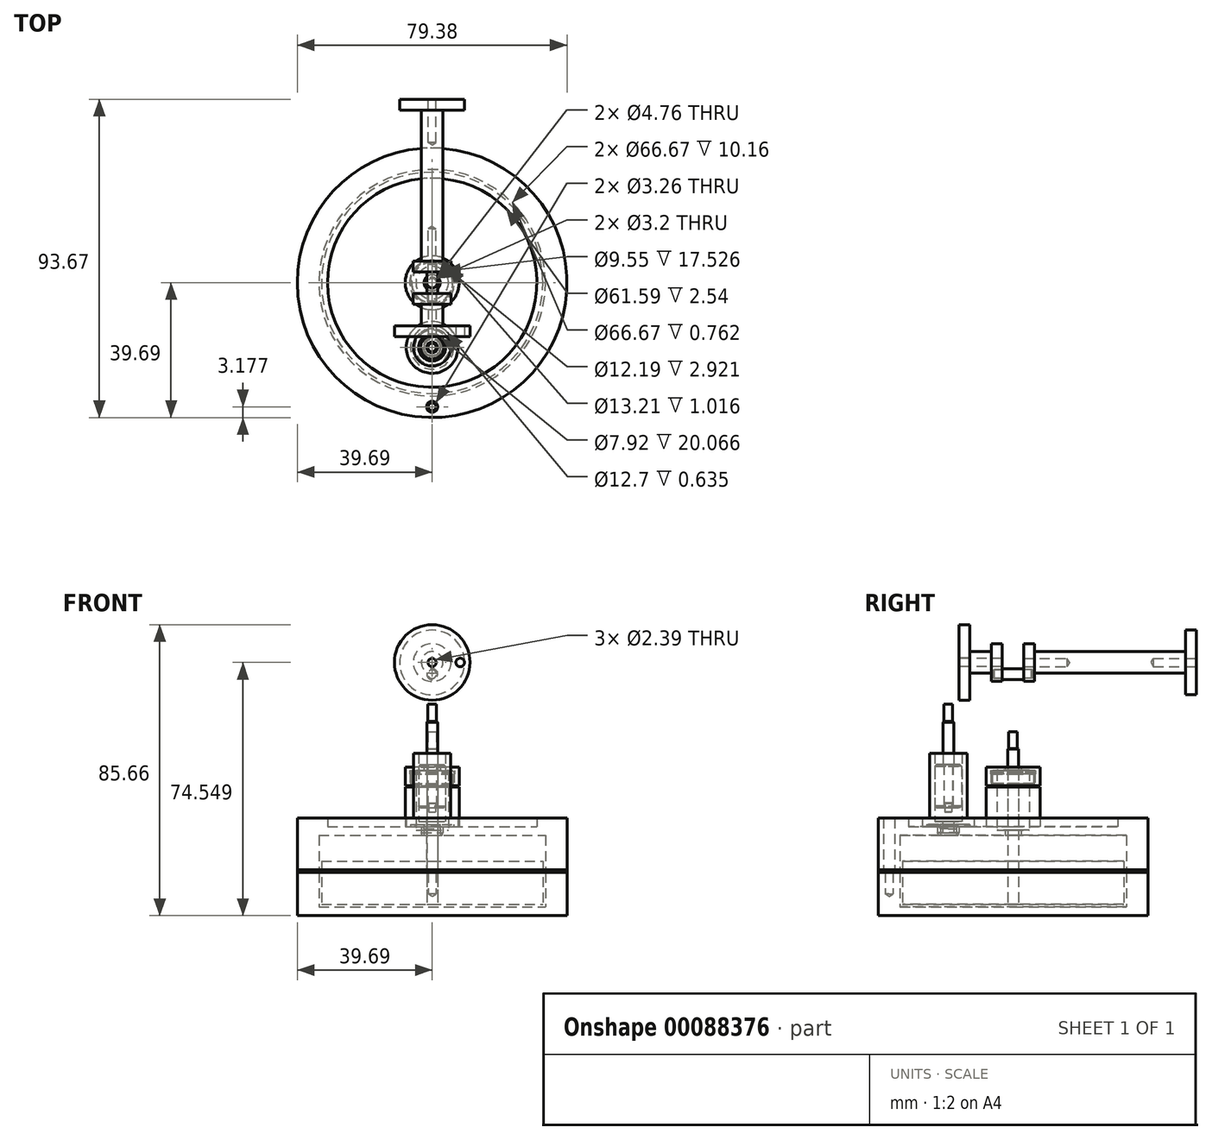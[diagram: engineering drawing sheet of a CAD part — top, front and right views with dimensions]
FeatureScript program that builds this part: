
annotation { "Feature Type Name" : "Feature", "Feature Type Description" : "" }
export const myFeature = defineFeature(function(context is Context, id is Id, definition is map)
    precondition{}
    {
        {
            assignVariable(context, id + "F0", {"name" : "RevolveDeg", "anyValue" : 360});
        }
        {
            var Q0;
            Q0=qCreatedBy(makeId("Right.planeOp"),FACE);
            var sketch = newSketch(context, id + "F1", { "sketchPlane" : qUnion([Q0])});
            skLineSegment(sketch, "E0", {"start": v(0, 0) * mm, "end": v(0, 183.81) * mm, "construction": true});
            skLineSegment(sketch, "E1", {"start": v(0, 0) * mm, "end": v(39.69, 0) * mm});
            skLineSegment(sketch, "E2", {"start": v(39.69, 12.7) * mm, "end": v(33.34, 12.7) * mm});
            skLineSegment(sketch, "E3", {"start": v(33.34, 12.7) * mm, "end": v(33.34, 2.54) * mm});
            skLineSegment(sketch, "E4", {"start": v(33.34, 2.54) * mm, "end": v(0, 2.54) * mm});
            skLineSegment(sketch, "E5", {"start": v(0, 2.54) * mm, "end": v(0, 0) * mm});
            skLineSegment(sketch, "E6", {"start": v(39.69, 12.7) * mm, "end": v(39.69, 0) * mm});
            skSolve(sketch);
        }
        {
            var Q0;
            Q0 = qSketchRegion(id + "F1", true);
            var Q1;
            Q1=sQuery(id+"F1.wireOp",EDGE,"E0");
            revolve(context, id + "F2", {"entities" : qUnion([Q0]), "axis" : qUnion([Q1]), "revolveType" : RevolveType.ONE_DIRECTION, "angle" : (getVariable(context, 'RevolveDeg')) * degree});
        }
        {
            var Q0;
            Q0=qCreatedBy(makeId("Right.planeOp"),FACE);
            var sketch = newSketch(context, id + "F3", { "sketchPlane" : qUnion([Q0])});
            skLineSegment(sketch, "E7", {"start": v(0, 0) * mm, "end": v(0, 44.02) * mm, "construction": true});
            skLineSegment(sketch, "E8.bottom", {"start": v(33.34, 13.46) * mm, "end": v(39.69, 13.46) * mm});
            skLineSegment(sketch, "E8.top", {"start": v(33.34, 12.7) * mm, "end": v(39.69, 12.7) * mm});
            skLineSegment(sketch, "E8.left", {"start": v(33.34, 13.46) * mm, "end": v(33.34, 12.7) * mm});
            skLineSegment(sketch, "E8.right", {"start": v(39.69, 13.46) * mm, "end": v(39.69, 12.7) * mm});
            skSolve(sketch);
        }
        {
            var Q0;
            Q0 = qSketchRegion(id + "F3", true);
            var Q1;
            Q1=sQuery(id+"F1.wireOp",EDGE,"E0");
            revolve(context, id + "F4", {"entities" : qUnion([Q0]), "axis" : qUnion([Q1]), "revolveType" : RevolveType.ONE_DIRECTION, "angle" : (getVariable(context, 'RevolveDeg')) * degree});
        }
        {
            var Q0;
            Q0=qCreatedBy(makeId("Right.planeOp"),FACE);
            var sketch = newSketch(context, id + "F5", { "sketchPlane" : qUnion([Q0])});
            skLineSegment(sketch, "E9", {"start": v(0, 0) * mm, "end": v(0, 65.3) * mm, "construction": true});
            skLineSegment(sketch, "E10", {"start": v(2.38, 23.62) * mm, "end": v(33.34, 23.62) * mm});
            skLineSegment(sketch, "E11", {"start": v(33.34, 23.62) * mm, "end": v(33.34, 13.46) * mm});
            skLineSegment(sketch, "E12", {"start": v(33.34, 13.46) * mm, "end": v(39.69, 13.46) * mm});
            skLineSegment(sketch, "E13", {"start": v(30.8, 26.16) * mm, "end": v(7.94, 26.16) * mm});
            skLineSegment(sketch, "E14", {"start": v(7.94, 26.16) * mm, "end": v(7.94, 37.85) * mm});
            skLineSegment(sketch, "E15", {"start": v(5.97, 42.67) * mm, "end": v(4.78, 42.67) * mm});
            skLineSegment(sketch, "E16", {"start": v(4.78, 42.67) * mm, "end": v(4.78, 25.15) * mm});
            skLineSegment(sketch, "E17", {"start": v(30.8, 28.7) * mm, "end": v(39.69, 28.7) * mm});
            skLineSegment(sketch, "E18", {"start": v(39.69, 28.7) * mm, "end": v(39.69, 13.46) * mm});
            skLineSegment(sketch, "E19", {"start": v(4.78, 25.15) * mm, "end": v(2.38, 25.15) * mm});
            skLineSegment(sketch, "E20", {"start": v(2.38, 25.15) * mm, "end": v(2.38, 23.62) * mm});
            skLineSegment(sketch, "E21", {"start": v(7.94, 37.85) * mm, "end": v(5.97, 37.85) * mm});
            skLineSegment(sketch, "E22", {"start": v(5.97, 37.85) * mm, "end": v(5.97, 38.86) * mm});
            skLineSegment(sketch, "E23", {"start": v(5.97, 38.86) * mm, "end": v(6.48, 38.86) * mm});
            skLineSegment(sketch, "E24", {"start": v(6.48, 38.86) * mm, "end": v(6.48, 42.16) * mm});
            skLineSegment(sketch, "E25", {"start": v(6.48, 42.16) * mm, "end": v(5.97, 42.67) * mm});
            skLineSegment(sketch, "E26", {"start": v(30.8, 26.16) * mm, "end": v(30.8, 28.7) * mm});
            skSolve(sketch);
        }
        {
            var Q0;
            Q0 = qSketchRegion(id + "F5", true);
            var Q1;
            Q1=sQuery(id+"F5.wireOp",EDGE,"E9");
            revolve(context, id + "F6", {"entities" : qUnion([Q0]), "axis" : qUnion([Q1]), "revolveType" : RevolveType.ONE_DIRECTION, "angle" : (getVariable(context, 'RevolveDeg')) * degree});
        }
        {
            var Q0;
            Q0=qCreatedBy(makeId("Right.planeOp"),FACE);
            var sketch = newSketch(context, id + "F7", { "sketchPlane" : qUnion([Q0])});
            skLineSegment(sketch, "E27", {"start": v(-19.05, 41.18) * mm, "end": v(-19.05, 9.69) * mm, "construction": true});
            skLineSegment(sketch, "E28", {"start": v(-19.05, 38.1) * mm, "end": v(-16.66, 38.1) * mm});
            skLineSegment(sketch, "E29", {"start": v(-16.66, 38.1) * mm, "end": v(-16.66, 19.05) * mm});
            skLineSegment(sketch, "E30", {"start": v(-16.66, 19.05) * mm, "end": v(-19.05, 19.05) * mm});
            skLineSegment(sketch, "E31", {"start": v(-19.05, 19.05) * mm, "end": v(-19.05, 38.1) * mm});
            skSolve(sketch);
        }
        {
            var Q0;
            Q0 = qSketchRegion(id + "F7", true);
            var Q1;
            Q1=sQuery(id+"F7.wireOp",EDGE,"E27");
            revolve(context, id + "F8", {"operationType" : NewBodyOperationType.REMOVE, "entities" : qUnion([Q0]), "axis" : qUnion([Q1]), "revolveType" : RevolveType.FULL, "oppositeDirection" : true});
        }
        {
            var Q0;
            Q0=makeQuery(id+"F8.boolean.opBoolean","INTERSECT",EDGE,{"derivedFrom":[makeQuery(id+"F6.opRevolve","SWEPT_FACE",FACE,{"disambiguationData":[OSD([sQuery(id+"F5.wireOp",EDGE,"E13")])]}),makeQuery(id+"F8.opRevolve","SWEPT_FACE",FACE,{"disambiguationData":[OSD([sQuery(id+"F7.wireOp",EDGE,"E29")])]})]});
            chamfer(context, id + "F9", {"entities" : qUnion([Q0]), "chamferType" : ChamferType.OFFSET_ANGLE, "width" : 0.2 * mm, "oppositeDirection" : false, "angle" : 70 * degree, "tangentPropagation" : true});
        }
        {
            var Q0;
            Q0=makeQuery(id+"F6.opRevolve","SWEPT_FACE",FACE,{"disambiguationData":[OSD([sQuery(id+"F5.wireOp",EDGE,"E17")])]});
            var sketch = newSketch(context, id + "F10", { "sketchPlane" : qUnion([Q0])});
            skLineSegment(sketch, "E32", {"start": v(0, 0) * mm, "end": v(0, -36.51) * mm, "construction": true});
            skSolve(sketch);
        }
        {
            var Q0;
            Q0=sQuery(id+"F10.wireOp",VERTEX,"E32.end");
            var Q1;
            Q1=makeQuery(id+"F6.opRevolve","SWEPT_BODY",BODY,{"disambiguationData":[OSD([sQuery(id+"F5.wireOp",EDGE,"E10"),sQuery(id+"F5.wireOp",EDGE,"E11"),sQuery(id+"F5.wireOp",EDGE,"E12"),sQuery(id+"F5.wireOp",EDGE,"08VaniDS-F7S3-UYdR-9gwU-UklKb1meRO1m"),sQuery(id+"F5.wireOp",EDGE,"E13"),sQuery(id+"F5.wireOp",EDGE,"E14"),sQuery(id+"F5.wireOp",EDGE,"E15"),sQuery(id+"F5.wireOp",EDGE,"E16"),sQuery(id+"F5.wireOp",EDGE,"E17"),sQuery(id+"F5.wireOp",EDGE,"E18"),sQuery(id+"F5.wireOp",EDGE,"E19"),sQuery(id+"F5.wireOp",EDGE,"E20"),sQuery(id+"F5.wireOp",EDGE,"E21"),sQuery(id+"F5.wireOp",EDGE,"E22"),sQuery(id+"F5.wireOp",EDGE,"E23"),sQuery(id+"F5.wireOp",EDGE,"E24"),sQuery(id+"F5.wireOp",EDGE,"E25"),sQuery(id+"F5.wireOp",EDGE,"E26"),sQuery(id+"F5.wireOp",EDGE,"p2X2xDUn-i6el-BxTP-Kqf6-1vIeUNN4H1RK")])]});
            hole(context, id + "F11", {"style" : HoleStyle.SIMPLE, "endStyle" : HoleEndStyle.THROUGH, "standardTappedOrClearance" : lookupTablePath({ "standard" : "ANSI", "fit" : "Normal (ASME)", "size" : "#4", "type" : "Clearance" }), "standardBlindInLast" : lookupTablePath({ "fit" : "Free", "standard" : "ANSI", "size" : "#4", "type" : "Clearance" }), "holeDiameter" : 3.26 * mm, "locations" : qUnion([Q0]), "scope" : qUnion([Q1]), "isTappedThrough" : true});
        }
        {
            var Q0;
            Q0=sQuery(id+"F10.wireOp",VERTEX,"E32.end");
            var Q1;
            Q1=makeQuery(id+"F4.opRevolve","SWEPT_BODY",BODY,{"disambiguationData":[OSD([sQuery(id+"F3.wireOp",EDGE,"E8.bottom"),sQuery(id+"F3.wireOp",EDGE,"E8.top"),sQuery(id+"F3.wireOp",EDGE,"E8.left"),sQuery(id+"F3.wireOp",EDGE,"E8.right")])]});
            hole(context, id + "F12", {"style" : HoleStyle.SIMPLE, "endStyle" : HoleEndStyle.THROUGH, "standardTappedOrClearance" : lookupTablePath({ "standard" : "ANSI", "fit" : "Normal (ASME)", "size" : "#4", "type" : "Clearance" }), "standardBlindInLast" : lookupTablePath({ "fit" : "Free", "standard" : "ANSI", "size" : "#4", "type" : "Clearance" }), "holeDiameter" : 3.26 * mm, "locations" : qUnion([Q0]), "scope" : qUnion([Q1]), "isTappedThrough" : true});
        }
        {
            var Q0;
            Q0=sQuery(id+"F10.wireOp",VERTEX,"E32.end");
            var Q1;
            Q1=makeQuery(id+"F2.opRevolve","SWEPT_BODY",BODY,{"disambiguationData":[OSD([sQuery(id+"F1.wireOp",EDGE,"E1"),sQuery(id+"F1.wireOp",EDGE,"E2"),sQuery(id+"F1.wireOp",EDGE,"E3"),sQuery(id+"F1.wireOp",EDGE,"E4"),sQuery(id+"F1.wireOp",EDGE,"E5"),sQuery(id+"F1.wireOp",EDGE,"E6")])]});
            hole(context, id + "F13", {"style" : HoleStyle.SIMPLE, "endStyle" : HoleEndStyle.BLIND, "standardTappedOrClearance" : lookupTablePath({ "standard" : "ANSI", "engagement" : "75%", "pitch" : "40 tpi", "size" : "#4", "type" : "Tapped" }), "standardBlindInLast" : lookupTablePath({ "standard" : "ANSI", "engagement" : "75%", "pitch" : "40 tpi", "size" : "#4", "type" : "Tapped" }), "holeDiameter" : 2.26 * mm, "holeDepth" : 6.35 * mm, "locations" : qUnion([Q0]), "scope" : qUnion([Q1]), "majorDiameter" : 2.84 * mm});
        }
        {
            var Q0;
            Q0=qCreatedBy(makeId("Right.planeOp"),FACE);
            var sketch = newSketch(context, id + "F14", { "sketchPlane" : qUnion([Q0])});
            skLineSegment(sketch, "E33", {"start": v(0, 0) * mm, "end": v(0, 53.04) * mm, "construction": true});
            skLineSegment(sketch, "E34.bottom", {"start": v(4.78, 25.15) * mm, "end": v(1.6, 25.15) * mm});
            skLineSegment(sketch, "E34.top", {"start": v(4.78, 42.8) * mm, "end": v(1.6, 42.8) * mm});
            skLineSegment(sketch, "E34.left", {"start": v(4.78, 25.15) * mm, "end": v(4.78, 42.8) * mm});
            skLineSegment(sketch, "E34.right", {"start": v(1.6, 25.15) * mm, "end": v(1.6, 42.8) * mm});
            skSolve(sketch);
        }
        {
            var Q0;
            Q0 = qSketchRegion(id + "F14", true);
            var Q1;
            Q1=sQuery(id+"F14.wireOp",EDGE,"E33");
            revolve(context, id + "F15", {"entities" : qUnion([Q0]), "axis" : qUnion([Q1]), "revolveType" : RevolveType.ONE_DIRECTION, "angle" : (getVariable(context, 'RevolveDeg')) * degree});
        }
        {
            var Q0;
            Q0=qCreatedBy(makeId("Right.planeOp"),FACE);
            var sketch = newSketch(context, id + "F16", { "sketchPlane" : qUnion([Q0])});
            skLineSegment(sketch, "E35", {"start": v(0, 0) * mm, "end": v(0, 48.97) * mm, "construction": true});
            skLineSegment(sketch, "E36", {"start": v(6.1, 38.74) * mm, "end": v(6.6, 38.23) * mm});
            skLineSegment(sketch, "E37", {"start": v(6.6, 38.23) * mm, "end": v(7.94, 38.23) * mm});
            skLineSegment(sketch, "E38", {"start": v(7.94, 38.23) * mm, "end": v(7.94, 43.69) * mm});
            skLineSegment(sketch, "E39", {"start": v(7.94, 43.69) * mm, "end": v(2.38, 43.69) * mm});
            skLineSegment(sketch, "E40", {"start": v(2.38, 43.69) * mm, "end": v(2.38, 42.67) * mm});
            skLineSegment(sketch, "E41", {"start": v(2.38, 42.67) * mm, "end": v(6.6, 42.67) * mm});
            skLineSegment(sketch, "E42", {"start": v(6.1, 41.66) * mm, "end": v(6.1, 38.74) * mm});
            skLineSegment(sketch, "E43", {"start": v(6.1, 41.66) * mm, "end": v(6.6, 41.66) * mm});
            skLineSegment(sketch, "E44", {"start": v(6.6, 41.66) * mm, "end": v(6.6, 42.67) * mm});
            skSolve(sketch);
        }
        {
            var Q0;
            Q0 = qSketchRegion(id + "F16", true);
            var Q1;
            Q1=sQuery(id+"F16.wireOp",EDGE,"E35");
            revolve(context, id + "F17", {"entities" : qUnion([Q0]), "axis" : qUnion([Q1]), "revolveType" : RevolveType.ONE_DIRECTION, "angle" : (getVariable(context, 'RevolveDeg')) * degree});
        }
        {
            var Q0;
            Q0=qCreatedBy(makeId("Right.planeOp"),FACE);
            var sketch = newSketch(context, id + "F18", { "sketchPlane" : qUnion([Q0])});
            skLineSegment(sketch, "E45", {"start": v(0, 0) * mm, "end": v(0, 54.6) * mm, "construction": true});
            skLineSegment(sketch, "E46.bottom", {"start": v(1.6, 3.3) * mm, "end": v(32.58, 3.3) * mm});
            skLineSegment(sketch, "E46.top", {"start": v(1.6, 16) * mm, "end": v(32.58, 16) * mm});
            skLineSegment(sketch, "E46.left", {"start": v(1.6, 3.3) * mm, "end": v(1.6, 16) * mm});
            skLineSegment(sketch, "E46.right", {"start": v(32.58, 3.3) * mm, "end": v(32.58, 16) * mm});
            skSolve(sketch);
        }
        {
            var Q0;
            Q0 = qSketchRegion(id + "F18", true);
            var Q1;
            Q1=sQuery(id+"F18.wireOp",EDGE,"E45");
            revolve(context, id + "F19", {"entities" : qUnion([Q0]), "axis" : qUnion([Q1]), "revolveType" : RevolveType.ONE_DIRECTION, "angle" : (getVariable(context, 'RevolveDeg')) * degree});
        }
        {
            var Q0;
            Q0=qCreatedBy(makeId("Right.planeOp"),FACE);
            var sketch = newSketch(context, id + "F20", { "sketchPlane" : qUnion([Q0])});
            skLineSegment(sketch, "E47", {"start": v(0, 0) * mm, "end": v(0, 67.1) * mm, "construction": true});
            skLineSegment(sketch, "E48.bottom", {"start": v(0, 3.3) * mm, "end": v(1.59, 3.3) * mm});
            skLineSegment(sketch, "E48.top", {"start": v(0, 54.1) * mm, "end": v(1.27, 54.1) * mm});
            skLineSegment(sketch, "E48.left", {"start": v(0, 3.3) * mm, "end": v(0, 54.1) * mm});
            skLineSegment(sketch, "E48.right", {"start": v(1.59, 3.3) * mm, "end": v(1.59, 49.02) * mm});
            skLineSegment(sketch, "E49", {"start": v(1.59, 49.02) * mm, "end": v(1.27, 49.2) * mm});
            skLineSegment(sketch, "E50", {"start": v(1.27, 49.2) * mm, "end": v(1.27, 54.1) * mm});
            skSolve(sketch);
        }
        {
            var Q0;
            Q0 = qSketchRegion(id + "F20", true);
            var Q1;
            Q1=sQuery(id+"F20.wireOp",EDGE,"E47");
            revolve(context, id + "F21", {"entities" : qUnion([Q0]), "axis" : qUnion([Q1]), "revolveType" : RevolveType.FULL});
        }
        {
            var Q0;
            Q0=qCreatedBy(makeId("Right.planeOp"),FACE);
            var sketch = newSketch(context, id + "F22", { "sketchPlane" : qUnion([Q0])});
            skLineSegment(sketch, "E51", {"start": v(-19.05, 59.37) * mm, "end": v(-19.05, -7.55) * mm, "construction": true});
            skLineSegment(sketch, "E52", {"start": v(-13.56, 47.75) * mm, "end": v(-13.56, 28.7) * mm});
            skLineSegment(sketch, "E53", {"start": v(-13.56, 28.7) * mm, "end": v(-11.43, 28.7) * mm});
            skLineSegment(sketch, "E54", {"start": v(-11.43, 28.7) * mm, "end": v(-11.43, 26.16) * mm});
            skLineSegment(sketch, "E55", {"start": v(-11.43, 26.16) * mm, "end": v(-12.7, 26.16) * mm});
            skLineSegment(sketch, "E56", {"start": v(-12.7, 26.16) * mm, "end": v(-12.7, 26.8) * mm});
            skLineSegment(sketch, "E57", {"start": v(-12.7, 26.8) * mm, "end": v(-13.97, 26.8) * mm});
            skLineSegment(sketch, "E58", {"start": v(-13.97, 26.8) * mm, "end": v(-13.97, 26.16) * mm});
            skLineSegment(sketch, "E59", {"start": v(-13.97, 26.16) * mm, "end": v(-15.88, 26.16) * mm});
            skLineSegment(sketch, "E60", {"start": v(-15.88, 26.16) * mm, "end": v(-15.88, 24.38) * mm});
            skLineSegment(sketch, "E61", {"start": v(-15.88, 24.38) * mm, "end": v(-16.15, 23.62) * mm});
            skLineSegment(sketch, "E62", {"start": v(-16.15, 23.62) * mm, "end": v(-17.4, 23.62) * mm});
            skLineSegment(sketch, "E63", {"start": v(-17.4, 23.62) * mm, "end": v(-17.4, 27.69) * mm});
            skLineSegment(sketch, "E64", {"start": v(-17.4, 27.69) * mm, "end": v(-15.09, 27.69) * mm});
            skLineSegment(sketch, "E65", {"start": v(-15.09, 27.69) * mm, "end": v(-15.09, 47.75) * mm});
            skLineSegment(sketch, "E66", {"start": v(-15.09, 47.75) * mm, "end": v(-13.56, 47.75) * mm});
            skSolve(sketch);
        }
        {
            var Q0;
            Q0 = qSketchRegion(id + "F22", true);
            var Q1;
            Q1=sQuery(id+"F22.wireOp",EDGE,"E51");
            revolve(context, id + "F23", {"entities" : qUnion([Q0]), "axis" : qUnion([Q1]), "revolveType" : RevolveType.ONE_DIRECTION, "oppositeDirection" : true, "angle" : (getVariable(context, 'RevolveDeg')) * degree});
        }
        {
            var Q0;
            Q0=qCreatedBy(makeId("Right.planeOp"),FACE);
            var sketch = newSketch(context, id + "F24", { "sketchPlane" : qUnion([Q0])});
            skLineSegment(sketch, "E67", {"start": v(-19.05, -7.77) * mm, "end": v(-19.05, 61.16) * mm, "construction": true});
            skLineSegment(sketch, "E68.bottom", {"start": v(-17.75, 31.75) * mm, "end": v(-15.11, 31.75) * mm});
            skLineSegment(sketch, "E68.top", {"start": v(-17.75, 44.45) * mm, "end": v(-15.11, 44.45) * mm});
            skLineSegment(sketch, "E68.left", {"start": v(-17.75, 31.75) * mm, "end": v(-17.75, 44.45) * mm});
            skLineSegment(sketch, "E68.right", {"start": v(-15.11, 31.75) * mm, "end": v(-15.11, 44.45) * mm});
            skSolve(sketch);
        }
        {
            var Q0;
            Q0 = qSketchRegion(id + "F24", true);
            var Q1;
            Q1=sQuery(id+"F24.wireOp",EDGE,"E67");
            revolve(context, id + "F25", {"entities" : qUnion([Q0]), "axis" : qUnion([Q1]), "revolveType" : RevolveType.ONE_DIRECTION, "angle" : (getVariable(context, 'RevolveDeg')) * degree});
        }
        {
            var Q0;
            Q0=makeQuery(id+"F25.opRevolve","SWEPT_EDGE",EDGE,{"disambiguationData":[OSD([sQuery(id+"F24.wireOp",EDGE,"E68.top"),sQuery(id+"F24.wireOp",EDGE,"E68.right")])]});
            var Q1;
            Q1=makeQuery(id+"F25.opRevolve","SWEPT_EDGE",EDGE,{"disambiguationData":[OSD([sQuery(id+"F24.wireOp",EDGE,"E68.bottom"),sQuery(id+"F24.wireOp",EDGE,"E68.right")])]});
            chamfer(context, id + "F26", {"entities" : qUnion([Q0, Q1]), "width" : 0.5 * mm});
        }
        {
            var Q0;
            Q0=qCreatedBy(makeId("Right.planeOp"),FACE);
            var sketch = newSketch(context, id + "F27", { "sketchPlane" : qUnion([Q0])});
            skLineSegment(sketch, "E69", {"start": v(-19.05, -10.62) * mm, "end": v(-19.05, 63.7) * mm, "construction": true});
            skLineSegment(sketch, "E70.bottom", {"start": v(-19.05, 30.48) * mm, "end": v(-18.03, 30.48) * mm});
            skLineSegment(sketch, "E70.left", {"start": v(-19.05, 30.48) * mm, "end": v(-19.05, 62.23) * mm});
            skLineSegment(sketch, "E70.right", {"start": v(-17.46, 44.45) * mm, "end": v(-17.46, 56.97) * mm});
            skLineSegment(sketch, "E71", {"start": v(-17.46, 56.97) * mm, "end": v(-17.78, 57.15) * mm});
            skLineSegment(sketch, "E72", {"start": v(-17.78, 57.15) * mm, "end": v(-17.78, 62.23) * mm});
            skLineSegment(sketch, "E73", {"start": v(-17.78, 62.23) * mm, "end": v(-19.05, 62.23) * mm});
            skLineSegment(sketch, "E74", {"start": v(-17.46, 44.45) * mm, "end": v(-17.78, 44.45) * mm});
            skLineSegment(sketch, "E75", {"start": v(-17.78, 44.45) * mm, "end": v(-17.78, 33.17) * mm});
            skLineSegment(sketch, "E76", {"start": v(-17.78, 33.17) * mm, "end": v(-18.03, 33.02) * mm});
            skLineSegment(sketch, "E77", {"start": v(-18.03, 33.02) * mm, "end": v(-18.03, 30.48) * mm});
            skSolve(sketch);
        }
        {
            var Q0;
            Q0 = qSketchRegion(id + "F27", true);
            var Q1;
            Q1=sQuery(id+"F27.wireOp",EDGE,"E69");
            revolve(context, id + "F28", {"entities" : qUnion([Q0]), "axis" : qUnion([Q1]), "revolveType" : RevolveType.ONE_DIRECTION, "angle" : 360 * degree});
        }
        {
            var Q0;
            Q0=qCreatedBy(makeId("Right.planeOp"),FACE);
            var sketch = newSketch(context, id + "F29", { "sketchPlane" : qUnion([Q0])});
            skLineSegment(sketch, "E78", {"start": v(-88.87, 74.55) * mm, "end": v(85.8, 74.55) * mm, "construction": true});
            skLineSegment(sketch, "E79", {"start": v(-19.05, -16.55) * mm, "end": v(-19.05, 125.12) * mm, "construction": true});
            skLineSegment(sketch, "E80", {"start": v(0, 0) * mm, "end": v(0, 126.37) * mm, "construction": true});
            skLineSegment(sketch, "E81", {"start": v(-15.88, 85.66) * mm, "end": v(-15.88, 75.74) * mm});
            skLineSegment(sketch, "E82", {"start": v(-15.88, 75.74) * mm, "end": v(-3.18, 75.74) * mm});
            skLineSegment(sketch, "E83", {"start": v(-3.18, 75.74) * mm, "end": v(-3.18, 80.1) * mm});
            skLineSegment(sketch, "E84", {"start": v(-3.18, 80.1) * mm, "end": v(-6.35, 80.1) * mm});
            skLineSegment(sketch, "E85", {"start": v(-6.35, 80.1) * mm, "end": v(-6.35, 77.72) * mm});
            skLineSegment(sketch, "E86", {"start": v(-6.35, 77.72) * mm, "end": v(-12.7, 77.72) * mm});
            skLineSegment(sketch, "E87", {"start": v(-12.7, 77.72) * mm, "end": v(-12.7, 85.66) * mm});
            skLineSegment(sketch, "E88", {"start": v(-12.7, 85.66) * mm, "end": v(-15.88, 85.66) * mm});
            skSolve(sketch);
        }
        {
            var Q0;
            Q0 = qSketchRegion(id + "F29", true);
            var Q1;
            Q1=sQuery(id+"F29.wireOp",EDGE,"E78");
            revolve(context, id + "F30", {"entities" : qUnion([Q0]), "axis" : qUnion([Q1]), "revolveType" : RevolveType.FULL});
        }
        {
            var Q0;
            Q0=makeQuery(id+"F30.opRevolve","SWEPT_FACE",FACE,{"disambiguationData":[OSD([sQuery(id+"F29.wireOp",EDGE,"E83")])]});
            var sketch = newSketch(context, id + "F31", { "sketchPlane" : qUnion([Q0])});
            skCircle(sketch, "E89", {"center": v(0, 71.12) * mm, "radius": 1.27 * mm});
            skLineSegment(sketch, "E90", {"start": v(0, 71.12) * mm, "end": v(0, 74.55) * mm, "construction": true});
            skLineSegment(sketch, "E91", {"start": v(0, 74.55) * mm, "end": v(20.69, 74.55) * mm, "construction": true});
            skSolve(sketch);
        }
        {
            var Q0;
            Q0 = qSketchRegion(id + "F31", true);
            extrude(context, id + "F32", {"entities" : qUnion([Q0]), "operationType" : NewBodyOperationType.REMOVE, "oppositeDirection" : true, "depth" : 2.54 * mm});
        }
        {
            var Q0;
            Q0=makeQuery(id+"F30.opRevolve","SWEPT_FACE",FACE,{"disambiguationData":[OSD([sQuery(id+"F29.wireOp",EDGE,"E81")])]});
            var sketch = newSketch(context, id + "F33", { "sketchPlane" : qUnion([Q0])});
            skLineSegment(sketch, "E92", {"start": v(0, 111.9) * mm, "end": v(0, 74.55) * mm, "construction": true});
            skLineSegment(sketch, "E93", {"start": v(0, 74.55) * mm, "end": v(8.26, 74.55) * mm, "construction": true});
            skCircle(sketch, "E94", {"center": v(8.26, 74.55) * mm, "radius": 1.27 * mm});
            skSolve(sketch);
        }
        {
            var Q0;
            Q0 = qSketchRegion(id + "F33", true);
            var Q1;
            Q1=sQuery(id+"F33.wireOp",EDGE,"E94");
            extrude(context, id + "F34", {"entities" : qUnion([Q0]), "operationType" : NewBodyOperationType.REMOVE, "surfaceEntities" : qUnion([Q1]), "oppositeDirection" : true, "depth" : 5.08 * mm});
        }
        {
            var Q0;
            Q0=qCreatedBy(makeId("Right.planeOp"),FACE);
            var sketch = newSketch(context, id + "F35", { "sketchPlane" : qUnion([Q0])});
            skLineSegment(sketch, "E95", {"start": v(3.18, 80.1) * mm, "end": v(3.18, 75.74) * mm});
            skLineSegment(sketch, "E96", {"start": v(3.18, 75.74) * mm, "end": v(15.88, 75.74) * mm});
            skLineSegment(sketch, "E97", {"start": v(53.98, 75.74) * mm, "end": v(53.98, 84.07) * mm});
            skLineSegment(sketch, "E98", {"start": v(53.98, 84.07) * mm, "end": v(50.8, 84.07) * mm});
            skLineSegment(sketch, "E99", {"start": v(50.8, 84.07) * mm, "end": v(50.8, 77.72) * mm});
            skLineSegment(sketch, "E100", {"start": v(50.8, 77.72) * mm, "end": v(6.35, 77.72) * mm});
            skLineSegment(sketch, "E101", {"start": v(6.35, 77.72) * mm, "end": v(6.35, 80.1) * mm});
            skLineSegment(sketch, "E102", {"start": v(6.35, 80.1) * mm, "end": v(3.18, 80.1) * mm});
            skLineSegment(sketch, "E103", {"start": v(0, 93.62) * mm, "end": v(0, 55.48) * mm, "construction": true});
            skLineSegment(sketch, "E104", {"start": v(86.06, 74.55) * mm, "end": v(-79.26, 74.55) * mm, "construction": true});
            skPoint(sketch, "E104.endSnap0", {"position": v(0, 74.55) * mm});
            skLineSegment(sketch, "E105", {"start": v(15.88, 75.74) * mm, "end": v(16.6, 74.55) * mm});
            skLineSegment(sketch, "E106", {"start": v(16.6, 74.55) * mm, "end": v(40.56, 74.55) * mm});
            skLineSegment(sketch, "E107", {"start": v(40.56, 74.55) * mm, "end": v(41.28, 75.74) * mm});
            skLineSegment(sketch, "E108.trimOffspring", {"start": v(41.28, 75.74) * mm, "end": v(53.98, 75.74) * mm});
            skSolve(sketch);
        }
        {
            var Q0;
            Q0 = qSketchRegion(id + "F35", true);
            var Q1;
            Q1=sQuery(id+"F35.wireOp",EDGE,"E104");
            revolve(context, id + "F36", {"entities" : qUnion([Q0]), "axis" : qUnion([Q1]), "revolveType" : RevolveType.FULL});
        }
        {
            var Q0;
            Q0=makeQuery(id+"F36.opRevolve","SWEPT_FACE",FACE,{"disambiguationData":[OSD([sQuery(id+"F35.wireOp",EDGE,"E95")])]});
            var sketch = newSketch(context, id + "F37", { "sketchPlane" : qUnion([Q0])});
            skCircle(sketch, "E109", {"center": v(0, 71.12) * mm, "radius": 1.27 * mm});
            skLineSegment(sketch, "E110", {"start": v(0, 71.12) * mm, "end": v(0, 74.55) * mm, "construction": true});
            skLineSegment(sketch, "E111", {"start": v(0, 74.55) * mm, "end": v(19.55, 74.55) * mm, "construction": true});
            skSolve(sketch);
        }
        {
            var Q0;
            Q0=makeQuery(id+"F37.imprint","IMPRINT",FACE,{"disambiguationData":[TD([[makeQuery(id+"F37.imprint","IMPRINT",EDGE,{"derivedFrom":sQuery(id+"F37.wireOp",EDGE,"E109")}),1.0]])]});
            extrude(context, id + "F38", {"entities" : qUnion([Q0]), "operationType" : NewBodyOperationType.REMOVE, "oppositeDirection" : true, "depth" : 2.54 * mm});
        }
        {
            var Q0;
            Q0=qCreatedBy(makeId("Right.planeOp"),FACE);
            var sketch = newSketch(context, id + "F39", { "sketchPlane" : qUnion([Q0])});
            skLineSegment(sketch, "E112", {"start": v(0, 0) * mm, "end": v(0, 135) * mm, "construction": true});
            skLineSegment(sketch, "E113", {"start": v(-47.28, 74.55) * mm, "end": v(75.1, 74.55) * mm, "construction": true});
            skLineSegment(sketch, "E114", {"start": v(-7.35, 71.12) * mm, "end": v(8.28, 71.12) * mm, "construction": true});
            skLineSegment(sketch, "E115", {"start": v(-5.46, 72.4) * mm, "end": v(-3.17, 72.4) * mm});
            skLineSegment(sketch, "E116", {"start": v(-3.17, 72.4) * mm, "end": v(-3.17, 72.7) * mm});
            skLineSegment(sketch, "E117", {"start": v(-3.17, 72.7) * mm, "end": v(3.17, 72.7) * mm});
            skLineSegment(sketch, "E118", {"start": v(3.18, 72.7) * mm, "end": v(3.18, 72.4) * mm});
            skLineSegment(sketch, "E119", {"start": v(3.17, 72.4) * mm, "end": v(5.46, 72.4) * mm});
            skLineSegment(sketch, "E120", {"start": v(5.46, 72.4) * mm, "end": v(5.46, 71.12) * mm});
            skLineSegment(sketch, "E121", {"start": v(5.46, 71.12) * mm, "end": v(-5.46, 71.12) * mm});
            skLineSegment(sketch, "E122", {"start": v(-5.46, 71.12) * mm, "end": v(-5.46, 72.4) * mm});
            skPoint(sketch, "E123", {"position": v(0, 72.7) * mm});
            skSolve(sketch);
        }
        {
            var Q0;
            Q0=makeQuery(id+"F39.imprint","IMPRINT",FACE,{"disambiguationData":[TD([[makeQuery(id+"F39.imprint","IMPRINT",EDGE,{"derivedFrom":sQuery(id+"F39.wireOp",EDGE,"E115")}),-1.0]])]});
            var Q1;
            Q1=sQuery(id+"F39.wireOp",EDGE,"E114");
            revolve(context, id + "F40", {"entities" : qUnion([Q0]), "axis" : qUnion([Q1]), "revolveType" : RevolveType.FULL});
        }
    });
